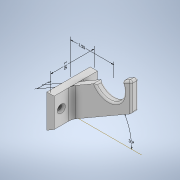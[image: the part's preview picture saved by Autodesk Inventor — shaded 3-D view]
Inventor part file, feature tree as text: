
AUTODESK INVENTOR PART (.ipt)
format: ipt  version: 2021.1 (Build 251245010, 245A)  size: 394,752 bytes
history: native  units: in
note: dims shown in document units (in); Inventor stores cm internally (conversion verified against a paired STEP export)
features: other x5, sketch x5, extrude x4, fillet x4, hole x1
ambient origin geometry x8: Origin, YZ Plane, XZ Plane, XY Plane, X Axis, Y Axis, Z Axis, Center Point
bodies: Solid2 (feature_tree)
feature tree (19):
  other  "Annotations"
  extrude  "Extrusion3"  Depth=0.25in
  extrude  "Extrusion4"  TaperAngle=30.0deg  [1 undecoded]
  sketch  "Sketch7"  dims[d26=1.075in d29=0.25in]
  extrude  "Extrusion5"  Depth=0.25in
  hole  "Hole3"  [1 undecoded]
  fillet  "Fillet3"  [1 undecoded]
  fillet  "Fillet4"  [1 undecoded]
  fillet  "Fillet5"  Radius=0.25in
  fillet  "Fillet6"  Radius=0.25in
  extrude  "Extrusion6"  Depth=0.0625in
  sketch  "Sketch5"  dims[d21=1.0in d22=0.25in]
  sketch  "Sketch6"  dims[d23=1.5in d24=0.0in d25=30.0deg]
  sketch  "Sketch8"  dims[d30=1.5in d31=0.25in d32=0.0in d33=0.0in d34=0.25in d35=0.25in]
  sketch  "Sketch9"  dims[d47=1.5in d48=0.0in d49=0.15in d50=0.75in d51=0.279in d52=0.25in d53=0.5635in d54=1.0in d55=0.8108in d65=0.0625in d66=0.0625in d67=0.0625in d68=0.125in d72=0.05in d73=0.0in d56=0.2085in d57=0.331in d58=1.5in d59=2.3174in d60=30.0deg d69=1.5in d70=0.3005in d71=0.25in]
  other  "Linear Dimension 1"
  other  "Angular Dimension 1"
  other  "Linear Dimension 2"
  other  "Linear Dimension 3"
note: 4 required parameter values undecoded (feature->parameter linkage not recoverable at this tier; creation-order binding heuristic only, values carry confidence <= 0.55)
